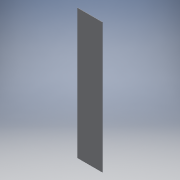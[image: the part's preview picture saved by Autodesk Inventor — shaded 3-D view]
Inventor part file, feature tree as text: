
AUTODESK INVENTOR PART (.ipt)
format: ipt  version: 2016 (Build 200138000, 138)  size: 88,576 bytes
history: native  units: in
note: dims shown in document units (in); Inventor stores cm internally (conversion verified against a paired STEP export)
features: extrude x1, sketch x1
ambient origin geometry x8: Origin, YZ Plane, XZ Plane, XY Plane, X Axis, Y Axis, Z Axis, Center Point
bodies: Solid1 (feature_tree)
feature tree (2):
  extrude  "Extrusion1"  Depth=21.0in
  sketch  "Sketch1"  dims[d0=4.0in d1=21.0in d2=0.0625in d3=0.0in]
